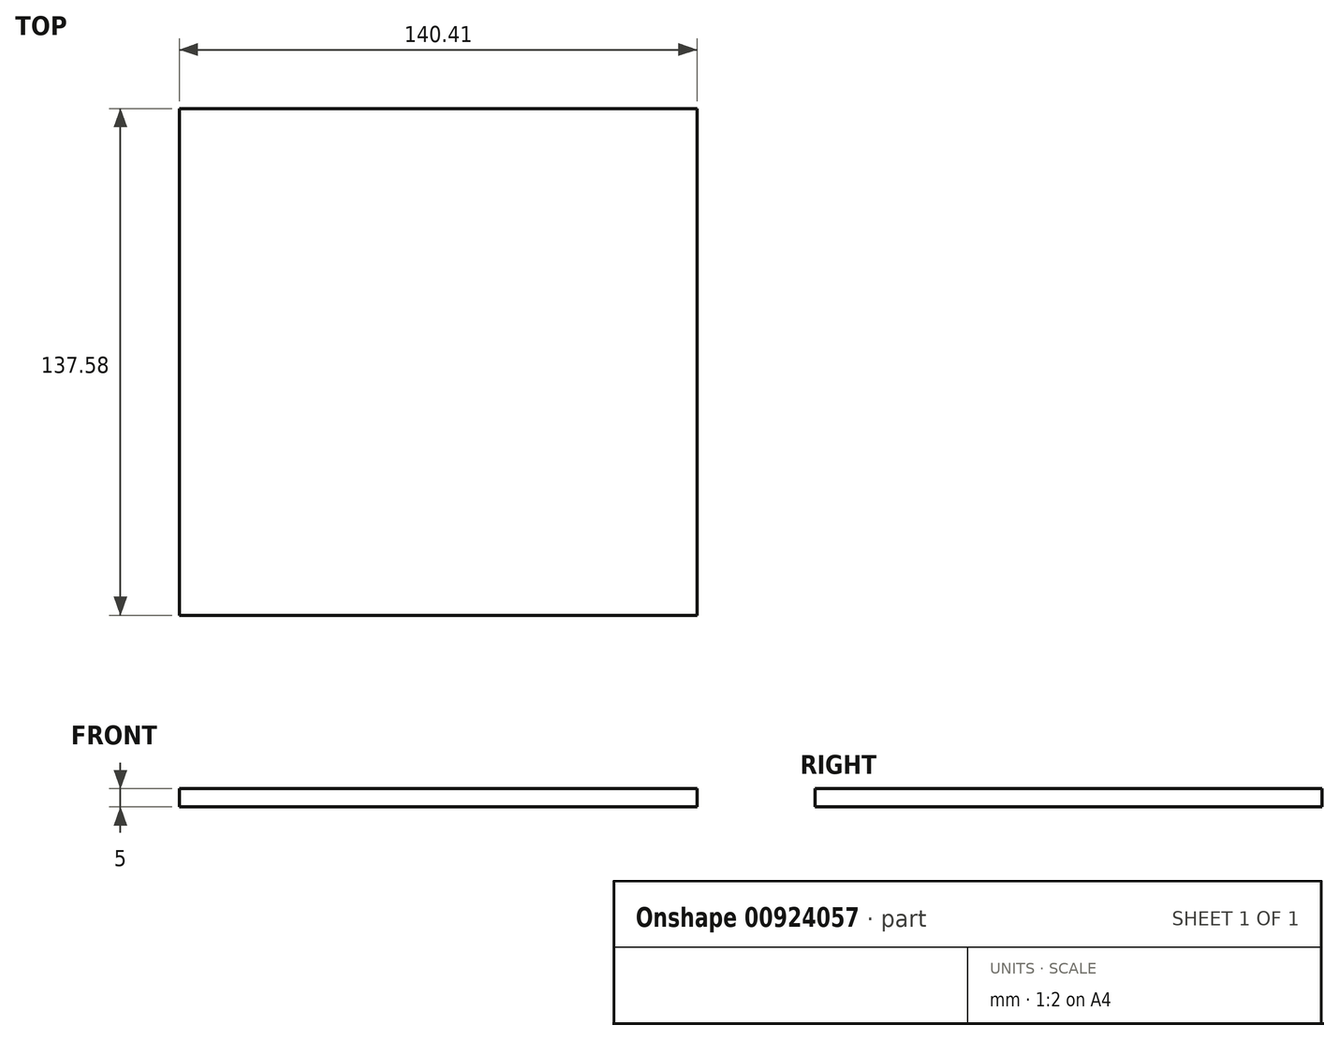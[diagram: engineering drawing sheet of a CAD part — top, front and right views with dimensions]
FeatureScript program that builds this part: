
annotation { "Feature Type Name" : "Feature", "Feature Type Description" : "" }
export const myFeature = defineFeature(function(context is Context, id is Id, definition is map)
    precondition{}
    {
        {
            var Q0;
            Q0=qCreatedBy(makeId("Top.planeOp"),FACE);
            var sketch = newSketch(context, id + "F0", { "sketchPlane" : qUnion([Q0])});
            skLineSegment(sketch, "E0.bottom", {"start": v(-71.33, 69.79) * mm, "end": v(69.08, 69.79) * mm});
            skLineSegment(sketch, "E0.top", {"start": v(-71.33, -67.8) * mm, "end": v(69.08, -67.8) * mm});
            skLineSegment(sketch, "E0.left", {"start": v(-71.33, 69.79) * mm, "end": v(-71.33, -67.8) * mm});
            skLineSegment(sketch, "E0.right", {"start": v(69.08, 69.79) * mm, "end": v(69.08, -67.8) * mm});
            skSolve(sketch);
        }
        {
            var Q0;
            Q0=makeQuery(id+"F0.imprint","IMPRINT",FACE,{"disambiguationData":[TD([[makeQuery(id+"F0.imprint","IMPRINT",EDGE,{"derivedFrom":sQuery(id+"F0.wireOp",EDGE,"E0.bottom")}),-1.0]])]});
            extrude(context, id + "F1", {"entities" : qUnion([Q0]), "depth" : 5 * mm, "offsetDistance" : 25.4 * mm});
        }
    });
